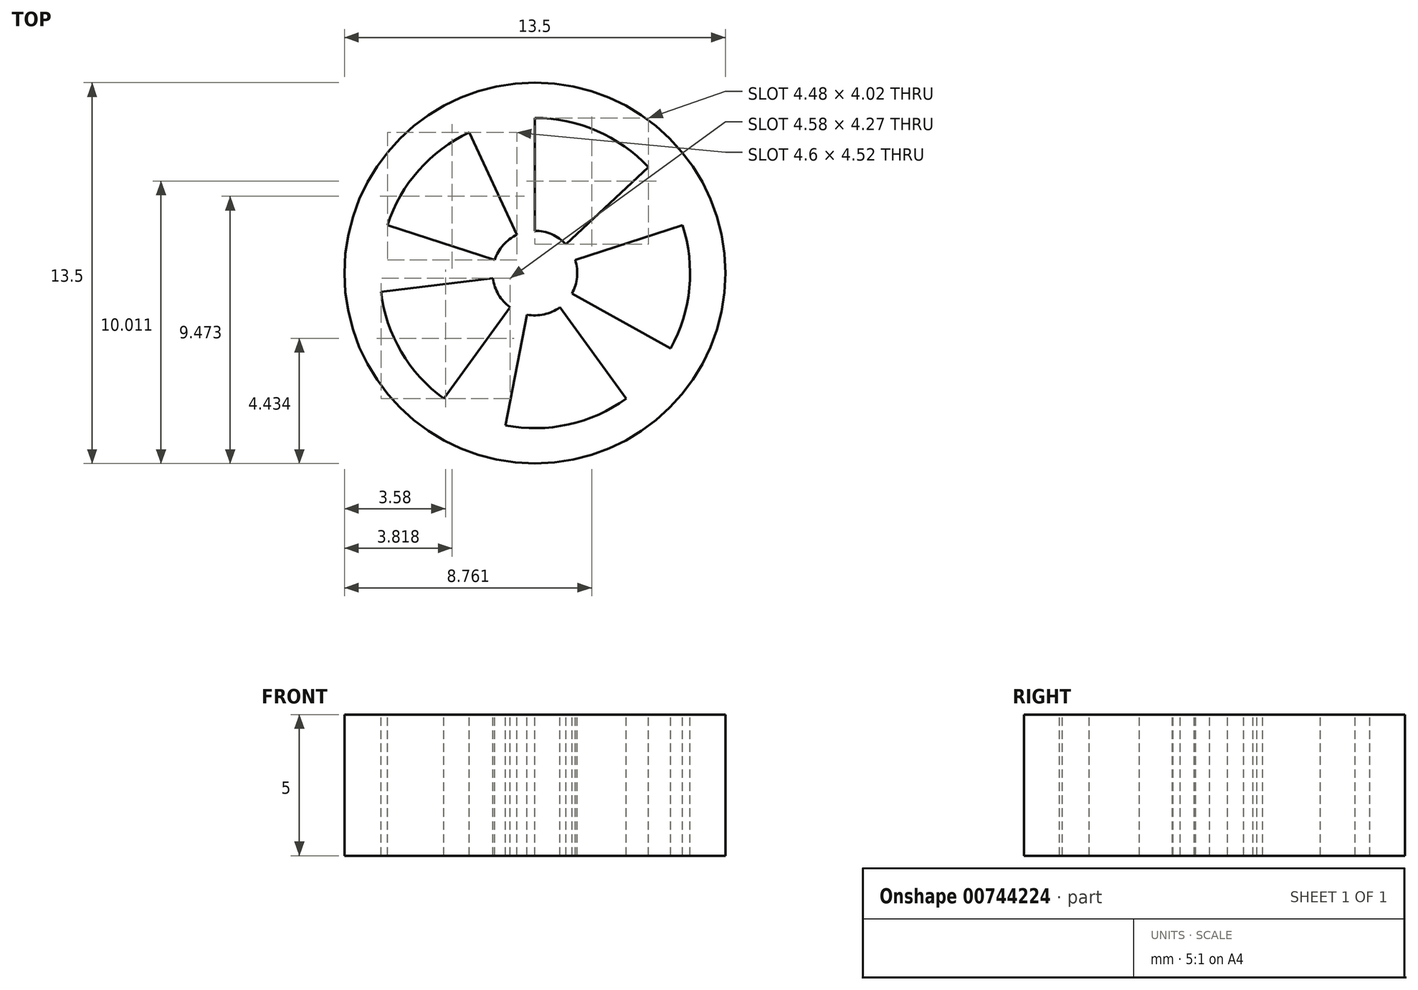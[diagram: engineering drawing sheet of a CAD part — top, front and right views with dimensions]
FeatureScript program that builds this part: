
annotation { "Feature Type Name" : "Feature", "Feature Type Description" : "" }
export const myFeature = defineFeature(function(context is Context, id is Id, definition is map)
    precondition{}
    {
        {
            var Q0;
            Q0=qCreatedBy(makeId("Top.planeOp"),FACE);
            var sketch = newSketch(context, id + "F0", { "sketchPlane" : qUnion([Q0])});
            skCircle(sketch, "E0", {"center": v(0, 0) * mm, "radius": 6.75 * mm});
            skSolve(sketch);
        }
        {
            var Q0;
            Q0=makeQuery(id+"F0.imprint","IMPRINT",FACE,{"disambiguationData":[TD([[makeQuery(id+"F0.imprint","IMPRINT",EDGE,{"derivedFrom":sQuery(id+"F0.wireOp",EDGE,"E0")}),1.0]])]});
            var Q1;
            Q1 = qSketchRegion(id + "F2", true);
            extrude(context, id + "F1", {"entities" : qUnion([Q0, Q1]), "depth" : 5 * mm, "offsetDistance" : 25 * mm});
        }
        {
            var Q0;
            Q0=makeQuery(id+"F1.opExtrude","CAP_FACE",FACE,{"disambiguationData":[OSD([sQuery(id+"F0.wireOp",EDGE,"E0")])],"isStart":false});
            var sketch = newSketch(context, id + "F2", { "sketchPlane" : qUnion([Q0])});
            skCircle(sketch, "E1", {"center": v(0, 0) * mm, "radius": 5.5 * mm});
            skCircle(sketch, "E2", {"center": v(0, 0) * mm, "radius": 1.5 * mm});
            skLineSegment(sketch, "E3", {"start": v(0, 5.5) * mm, "end": v(0, 1.5) * mm});
            skLineSegment(sketch, "E4", {"start": v(-2.32, 4.98) * mm, "end": v(-0.63, 1.36) * mm});
            skLineSegment(sketch, "E5.trimOffspring", {"start": v(0, 0) * mm, "end": v(0, -0.2) * mm});
            skLineSegment(sketch, "E6.1.0", {"start": v(-5.46, -0.67) * mm, "end": v(-1.49, -0.18) * mm});
            skLineSegment(sketch, "E6.1.1", {"start": v(-5.23, 1.7) * mm, "end": v(-1.43, 0.46) * mm});
            skLineSegment(sketch, "E6.2.0", {"start": v(-1.05, -5.4) * mm, "end": v(-0.29, -1.47) * mm});
            skLineSegment(sketch, "E6.2.1", {"start": v(-3.23, -4.45) * mm, "end": v(-0.88, -1.21) * mm});
            skLineSegment(sketch, "E6.3.0", {"start": v(4.8, -2.67) * mm, "end": v(1.31, -0.73) * mm});
            skLineSegment(sketch, "E6.3.1", {"start": v(3.23, -4.45) * mm, "end": v(0.88, -1.21) * mm});
            skLineSegment(sketch, "E6.4.0", {"start": v(4.02, 3.75) * mm, "end": v(1.1, 1.02) * mm});
            skLineSegment(sketch, "E6.4.1", {"start": v(5.23, 1.7) * mm, "end": v(1.43, 0.46) * mm});
            skSolve(sketch);
        }
        {
            var Q0;
            {var subQ0=sQuery(id+"F2.wireOp",EDGE,"E3");Q0=makeQuery(id+"F2.imprint","IMPRINT",FACE,{"disambiguationData":[TD([[makeQuery(id+"F2.imprint","IMPRINT",EDGE,{"derivedFrom":subQ0}),1.0]])]});}
            var Q1;
            {var subQ0=sQuery(id+"F2.wireOp",EDGE,"E4");Q1=makeQuery(id+"F2.imprint","IMPRINT",FACE,{"disambiguationData":[TD([[makeQuery(id+"F2.imprint","IMPRINT",EDGE,{"derivedFrom":subQ0}),-1.0]])]});}
            var Q2;
            {var subQ0=sQuery(id+"F2.wireOp",EDGE,"E6.1.0");Q2=makeQuery(id+"F2.imprint","IMPRINT",FACE,{"disambiguationData":[TD([[makeQuery(id+"F2.imprint","IMPRINT",EDGE,{"derivedFrom":subQ0}),-1.0]])]});}
            var Q3;
            {var subQ0=sQuery(id+"F2.wireOp",EDGE,"E6.2.0");Q3=makeQuery(id+"F2.imprint","IMPRINT",FACE,{"disambiguationData":[TD([[makeQuery(id+"F2.imprint","IMPRINT",EDGE,{"derivedFrom":subQ0}),-1.0]])]});}
            var Q4;
            {var subQ0=sQuery(id+"F2.wireOp",EDGE,"E6.3.0");Q4=makeQuery(id+"F2.imprint","IMPRINT",FACE,{"disambiguationData":[TD([[makeQuery(id+"F2.imprint","IMPRINT",EDGE,{"derivedFrom":subQ0}),-1.0]])]});}
            extrude(context, id + "F3", {"entities" : qUnion([Q0, Q1, Q2, Q3, Q4]), "operationType" : NewBodyOperationType.REMOVE, "oppositeDirection" : true, "depth" : 25 * mm, "offsetDistance" : 25 * mm});
        }
    });
